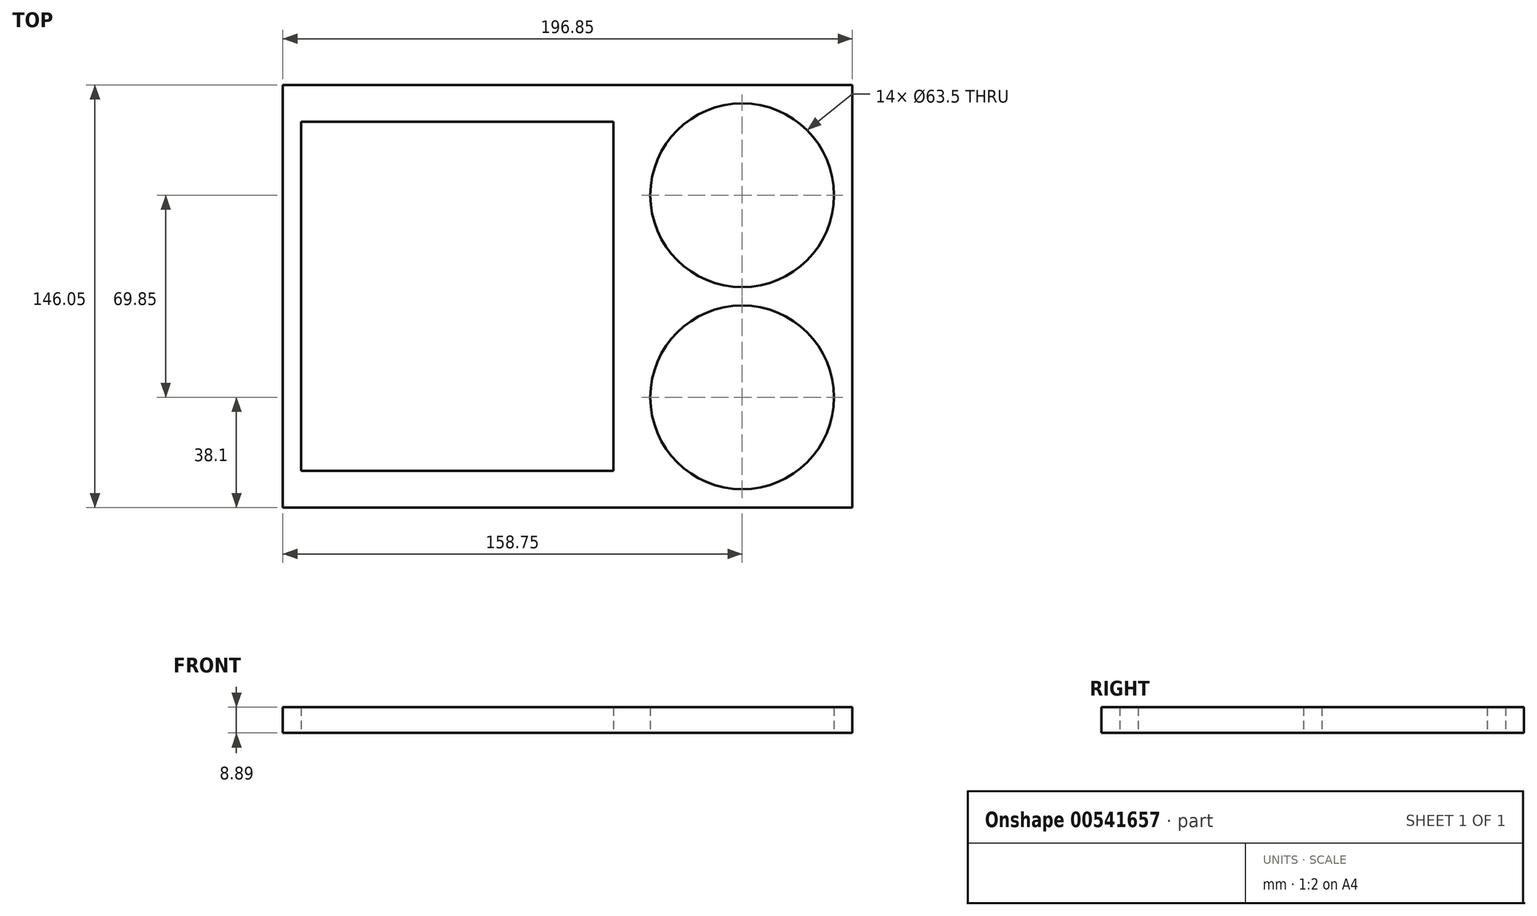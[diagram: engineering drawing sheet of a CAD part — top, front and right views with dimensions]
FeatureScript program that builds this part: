
annotation { "Feature Type Name" : "Feature", "Feature Type Description" : "" }
export const myFeature = defineFeature(function(context is Context, id is Id, definition is map)
    precondition{}
    {
        {
            var Q0;
            Q0=qCreatedBy(makeId("Top.planeOp"),FACE);
            var sketch = newSketch(context, id + "F0", { "sketchPlane" : qUnion([Q0])});
            skLineSegment(sketch, "E0.bottom", {"start": v(0, 0) * mm, "end": v(196.85, 0) * mm});
            skLineSegment(sketch, "E0.top", {"start": v(0, -146.05) * mm, "end": v(196.85, -146.05) * mm});
            skLineSegment(sketch, "E0.left", {"start": v(0, 0) * mm, "end": v(0, -146.05) * mm});
            skLineSegment(sketch, "E0.right", {"start": v(196.85, 0) * mm, "end": v(196.85, -146.05) * mm});
            skLineSegment(sketch, "E1.bottom", {"start": v(6.35, -12.7) * mm, "end": v(114.3, -12.7) * mm});
            skLineSegment(sketch, "E1.top", {"start": v(6.35, -133.35) * mm, "end": v(114.3, -133.35) * mm});
            skLineSegment(sketch, "E1.left", {"start": v(6.35, -12.7) * mm, "end": v(6.35, -133.35) * mm});
            skLineSegment(sketch, "E1.right", {"start": v(114.3, -12.7) * mm, "end": v(114.3, -133.35) * mm});
            skCircle(sketch, "E2", {"center": v(158.75, -38.1) * mm, "radius": 31.75 * mm});
            skCircle(sketch, "E3", {"center": v(158.75, -107.95) * mm, "radius": 31.75 * mm});
            skSolve(sketch);
        }
        {
            var Q0;
            Q0=makeQuery(id+"F0.imprint","IMPRINT",FACE,{"disambiguationData":[TD([[makeQuery(id+"F0.imprint","IMPRINT",EDGE,{"derivedFrom":sQuery(id+"F0.wireOp",EDGE,"E0.bottom")}),-1.0]])]});
            extrude(context, id + "F1", {"entities" : qUnion([Q0]), "depth" : 8.9 * mm, "offsetDistance" : 25.4 * mm});
        }
    });
